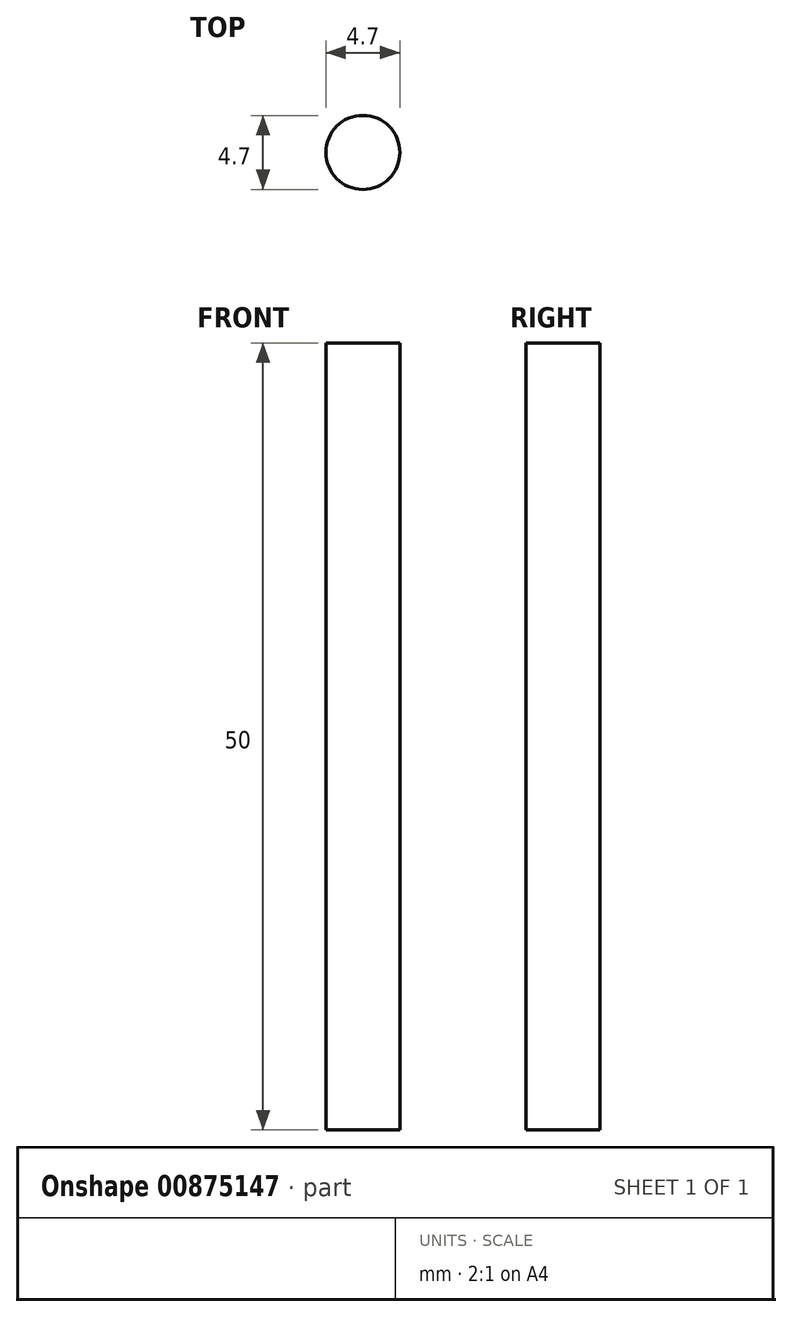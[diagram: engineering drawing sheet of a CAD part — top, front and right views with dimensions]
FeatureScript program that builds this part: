
annotation { "Feature Type Name" : "Feature", "Feature Type Description" : "" }
export const myFeature = defineFeature(function(context is Context, id is Id, definition is map)
    precondition{}
    {
        {
            var Q0;
            Q0=qCreatedBy(makeId("Top.planeOp"),FACE);
            var sketch = newSketch(context, id + "F0", { "sketchPlane" : qUnion([Q0])});
            skCircle(sketch, "E0", {"center": v(0, 0) * mm, "radius": 2.35 * mm});
            skSolve(sketch);
        }
        {
            var Q0;
            Q0 = qSketchRegion(id + "F0", true);
            extrude(context, id + "F1", {"entities" : qUnion([Q0]), "depth" : 50 * mm, "offsetDistance" : 25 * mm});
        }
    });
